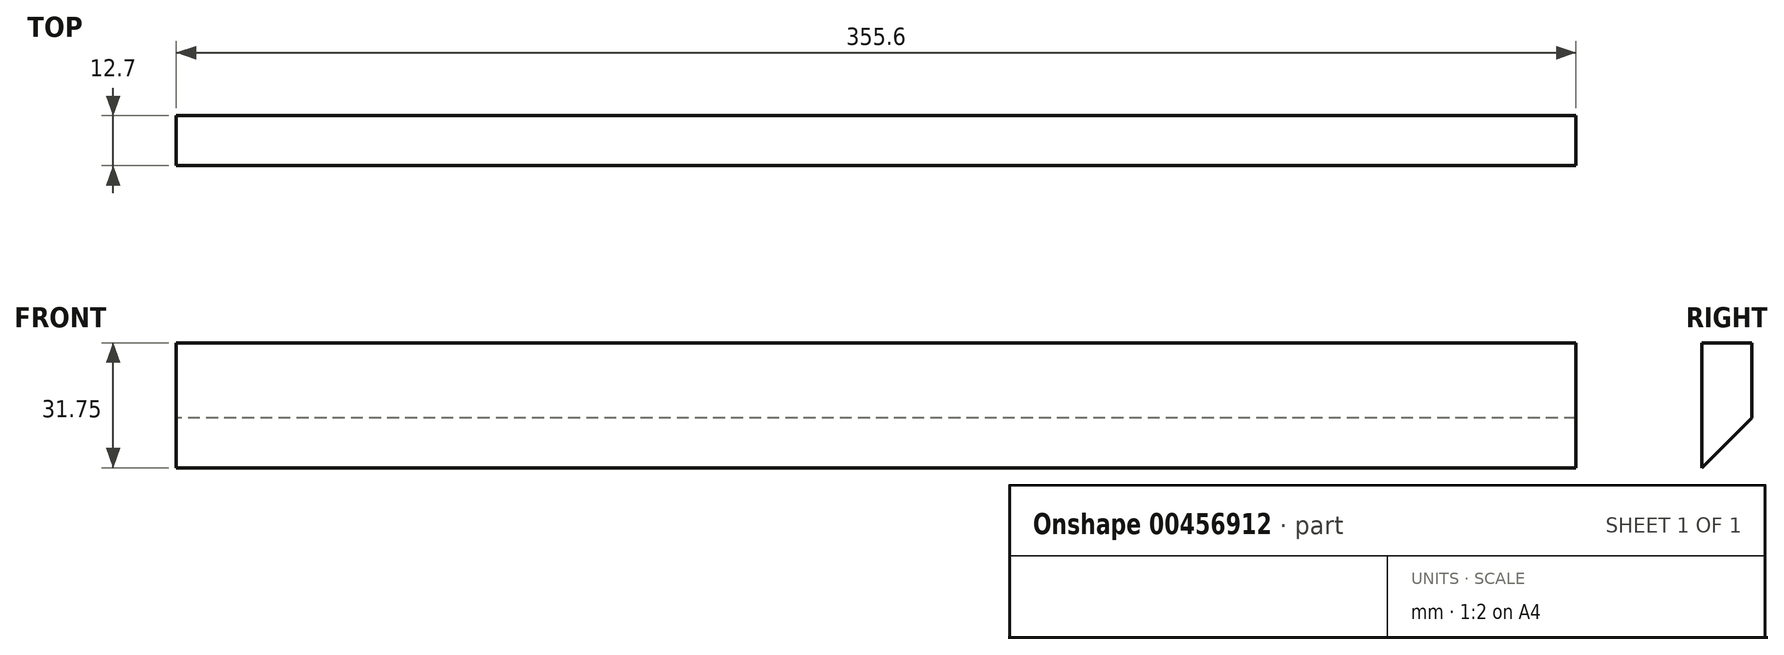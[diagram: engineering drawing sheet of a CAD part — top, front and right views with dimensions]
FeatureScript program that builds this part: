
annotation { "Feature Type Name" : "Feature", "Feature Type Description" : "" }
export const myFeature = defineFeature(function(context is Context, id is Id, definition is map)
    precondition{}
    {
        {
            var Q0;
            Q0=qCreatedBy(makeId("Right.planeOp"),FACE);
            var sketch = newSketch(context, id + "F0", { "sketchPlane" : qUnion([Q0])});
            skLineSegment(sketch, "E0.bottom", {"start": v(-7.86, 7.4) * mm, "end": v(4.84, 7.4) * mm});
            skLineSegment(sketch, "E0.left", {"start": v(-7.86, 7.4) * mm, "end": v(-7.86, -24.34) * mm});
            skLineSegment(sketch, "E0.right", {"start": v(4.84, 7.4) * mm, "end": v(4.84, -11.64) * mm});
            skLineSegment(sketch, "E1", {"start": v(-7.86, -24.34) * mm, "end": v(4.84, -11.64) * mm});
            skSolve(sketch);
        }
        {
            var Q0;
            Q0=makeQuery(id+"F0.imprint","IMPRINT",FACE,{"disambiguationData":[TD([[makeQuery(id+"F0.imprint","IMPRINT",EDGE,{"derivedFrom":sQuery(id+"F0.wireOp",EDGE,"E0.bottom")}),-1.0]])]});
            extrude(context, id + "F1", {"entities" : qUnion([Q0]), "depth" : 355.6 * mm});
        }
    });
